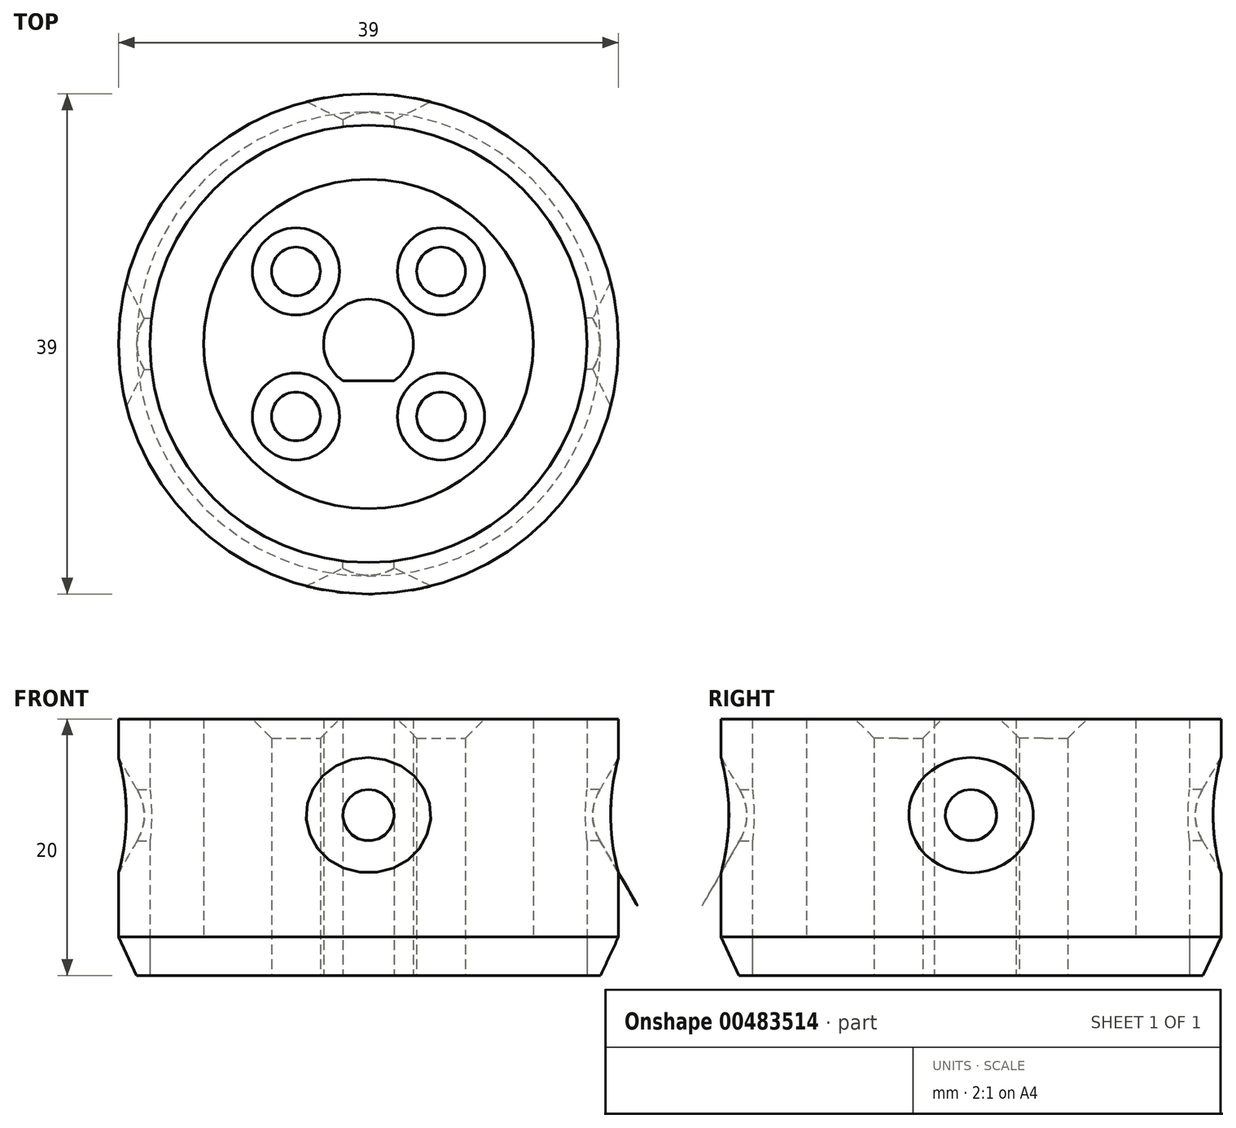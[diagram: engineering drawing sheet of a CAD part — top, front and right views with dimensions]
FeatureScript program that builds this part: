
annotation { "Feature Type Name" : "Feature", "Feature Type Description" : "" }
export const myFeature = defineFeature(function(context is Context, id is Id, definition is map)
    precondition{}
    {
        {
            var Q0;
            Q0=qCreatedBy(makeId("Top.planeOp"),FACE);
            var sketch = newSketch(context, id + "F0", { "sketchPlane" : qUnion([Q0])});
            skCircle(sketch, "E0", {"center": v(0, 0) * mm, "radius": 17.05 * mm});
            skCircle(sketch, "E1", {"center": v(0, 0) * mm, "radius": 3.35 * mm});
            skLineSegment(sketch, "E2", {"start": v(-2.3, -2.44) * mm, "end": v(1.68, -2.9) * mm});
            skSolve(sketch);
        }
        {
            var Q0;
            Q0=makeQuery(id+"F0.imprint","IMPRINT",FACE,{"disambiguationData":[TD([[makeQuery(id+"F0.imprint","IMPRINT",EDGE,{"derivedFrom":sQuery(id+"F0.wireOp",EDGE,"E0")}),1.0]])]});
            var sketch = newSketch(context, id + "F1", { "sketchPlane" : qUnion([Q0])});
            skCircle(sketch, "E3", {"center": v(0, 0) * mm, "radius": 19.5 * mm});
            skSolve(sketch);
        }
        {
            var Q0;
            Q0=makeQuery(id+"F1.imprint","IMPRINT",FACE,{"disambiguationData":[TD([[makeQuery(id+"F1.imprint","IMPRINT",EDGE,{"derivedFrom":sQuery(id+"F1.wireOp",EDGE,"E3")}),1.0]])]});
            var Q1;
            Q1=makeQuery(id+"F0.imprint","IMPRINT",FACE,{"disambiguationData":[TD([[makeQuery(id+"F0.imprint","IMPRINT",EDGE,{"derivedFrom":sQuery(id+"F0.wireOp",EDGE,"E0")}),1.0]])]});
            var Q2;
            {var subQ0=sQuery(id+"F0.wireOp",EDGE,"E2");Q2=makeQuery(id+"F0.imprint","IMPRINT",FACE,{"disambiguationData":[TD([[makeQuery(id+"F0.imprint","IMPRINT",EDGE,{"derivedFrom":subQ0}),1.0]])]});}
            var Q3;
            {var subQ0=sQuery(id+"F0.wireOp",EDGE,"E2");Q3=makeQuery(id+"F0.imprint","IMPRINT",FACE,{"disambiguationData":[TD([[makeQuery(id+"F0.imprint","IMPRINT",EDGE,{"derivedFrom":subQ0}),-1.0]])]});}
            extrude(context, id + "F2", {"entities" : qUnion([Q0, Q1, Q2, Q3]), "depth" : 20 * mm});
        }
        {
            var Q0;
            Q0=makeQuery(id+"F2.opExtrude","CAP_FACE",FACE,{"disambiguationData":[OSD([sQuery(id+"F0.wireOp",EDGE,"E0")])],"isStart":false});
            extrude(context, id + "F3", {"entities" : qUnion([Q0]), "operationType" : NewBodyOperationType.REMOVE, "oppositeDirection" : true, "depth" : 17 * mm});
        }
        {
            var Q0;
            Q0=makeQuery(id+"F2.opExtrude","CAP_FACE",FACE,{"disambiguationData":[OSD([sQuery(id+"F0.wireOp",EDGE,"E0")])],"isStart":true});
            var sketch = newSketch(context, id + "F4", { "sketchPlane" : qUnion([Q0])});
            skCircle(sketch, "E4", {"center": v(0, 0) * mm, "radius": 3.5 * mm});
            skLineSegment(sketch, "E5", {"start": v(-2, 2.87) * mm, "end": v(2, 2.87) * mm});
            skLineSegment(sketch, "E6", {"start": v(3.5, 0) * mm, "end": v(-3.5, 0) * mm, "construction": true});
            skSolve(sketch);
        }
        {
            var Q0;
            {var subQ0=sQuery(id+"F4.wireOp",EDGE,"E5");Q0=makeQuery(id+"F4.imprint","IMPRINT",FACE,{"disambiguationData":[TD([[makeQuery(id+"F4.imprint","IMPRINT",EDGE,{"derivedFrom":subQ0}),-1.0]])]});}
            extrude(context, id + "F5", {"entities" : qUnion([Q0]), "operationType" : NewBodyOperationType.REMOVE, "oppositeDirection" : true, "depth" : 9 * mm});
        }
        {
            var Q0;
            Q0=makeQuery(id+"F2.opExtrude","CAP_FACE",FACE,{"disambiguationData":[OSD([sQuery(id+"F0.wireOp",EDGE,"E0")])],"isStart":true});
            var sketch = newSketch(context, id + "F6", { "sketchPlane" : qUnion([Q0])});
            skLineSegment(sketch, "E7", {"start": v(0, 0) * mm, "end": v(-8, 0) * mm});
            skLineSegment(sketch, "E8", {"start": v(0, 0) * mm, "end": v(0, 8) * mm});
            skLineSegment(sketch, "E9", {"start": v(0, 0) * mm, "end": v(-5.66, 5.66) * mm});
            skLineSegment(sketch, "E10", {"start": v(0, 0) * mm, "end": v(5.66, -5.66) * mm});
            skLineSegment(sketch, "E11", {"start": v(0, 0) * mm, "end": v(-5.66, -5.66) * mm});
            skLineSegment(sketch, "E12", {"start": v(0, 0) * mm, "end": v(5.66, 5.66) * mm});
            skCircle(sketch, "E13", {"center": v(-5.66, 5.66) * mm, "radius": 1.9 * mm});
            skCircle(sketch, "E14", {"center": v(-5.66, -5.66) * mm, "radius": 1.9 * mm});
            skCircle(sketch, "E15", {"center": v(5.66, 5.66) * mm, "radius": 1.9 * mm});
            skCircle(sketch, "E16", {"center": v(5.66, -5.66) * mm, "radius": 1.9 * mm});
            skSolve(sketch);
        }
        {
            var Q0;
            Q0=makeQuery(id+"F6.imprint","IMPRINT",FACE,{"disambiguationData":[TD([[makeQuery(id+"F6.imprint","IMPRINT",EDGE,{"derivedFrom":sQuery(id+"F6.wireOp",EDGE,"E13")}),1.0]])]});
            var Q1;
            Q1=makeQuery(id+"F6.imprint","IMPRINT",FACE,{"disambiguationData":[TD([[makeQuery(id+"F6.imprint","IMPRINT",EDGE,{"derivedFrom":sQuery(id+"F6.wireOp",EDGE,"E14")}),1.0]])]});
            var Q2;
            Q2=makeQuery(id+"F6.imprint","IMPRINT",FACE,{"disambiguationData":[TD([[makeQuery(id+"F6.imprint","IMPRINT",EDGE,{"derivedFrom":sQuery(id+"F6.wireOp",EDGE,"E15")}),1.0]])]});
            var Q3;
            Q3=makeQuery(id+"F6.imprint","IMPRINT",FACE,{"disambiguationData":[TD([[makeQuery(id+"F6.imprint","IMPRINT",EDGE,{"derivedFrom":sQuery(id+"F6.wireOp",EDGE,"E16")}),1.0]])]});
            extrude(context, id + "F7", {"entities" : qUnion([Q0, Q1, Q2, Q3]), "operationType" : NewBodyOperationType.REMOVE, "oppositeDirection" : true, "depth" : 9 * mm});
        }
        {
            var Q0;
            Q0=qCreatedBy(makeId("Front.planeOp"),FACE);
            var sketch = newSketch(context, id + "F8", { "sketchPlane" : qUnion([Q0])});
            skLineSegment(sketch, "E17", {"start": v(0, 0) * mm, "end": v(0, 25) * mm});
            skCircle(sketch, "E18", {"center": v(0, 12.5) * mm, "radius": 2 * mm});
            skSolve(sketch);
        }
        {
            var Q0;
            Q0=qSketchRegion(id+"F8",true);
            extrude(context, id + "F9", {"entities" : qUnion([Q0]), "operationType" : NewBodyOperationType.REMOVE, "endBound" : BoundingType.THROUGH_ALL, "oppositeDirection" : true, "depth" : 25 * mm});
        }
        {
            var Q0;
            Q0=qCreatedBy(makeId("Front.planeOp"),FACE);
            var sketch = newSketch(context, id + "F10", { "sketchPlane" : qUnion([Q0])});
            skLineSegment(sketch, "E19", {"start": v(0, 0) * mm, "end": v(0, 25) * mm});
            skCircle(sketch, "E20", {"center": v(0, 12.5) * mm, "radius": 2 * mm});
            skSolve(sketch);
        }
        {
            var Q0;
            Q0=qSketchRegion(id+"F10",true);
            extrude(context, id + "F11", {"entities" : qUnion([Q0]), "operationType" : NewBodyOperationType.REMOVE, "endBound" : BoundingType.THROUGH_ALL, "depth" : 25 * mm});
        }
        {
            var Q0;
            Q0=qCreatedBy(makeId("Right.planeOp"),FACE);
            var sketch = newSketch(context, id + "F12", { "sketchPlane" : qUnion([Q0])});
            skLineSegment(sketch, "E21", {"start": v(0, 0) * mm, "end": v(0, 25) * mm});
            skCircle(sketch, "E22", {"center": v(0, 12.5) * mm, "radius": 2 * mm});
            skSolve(sketch);
        }
        {
            var Q0;
            Q0=qSketchRegion(id+"F12",true);
            extrude(context, id + "F13", {"entities" : qUnion([Q0]), "operationType" : NewBodyOperationType.REMOVE, "endBound" : BoundingType.THROUGH_ALL, "oppositeDirection" : true, "depth" : 25 * mm});
        }
        {
            var Q0;
            Q0=qCreatedBy(makeId("Right.planeOp"),FACE);
            var sketch = newSketch(context, id + "F14", { "sketchPlane" : qUnion([Q0])});
            skLineSegment(sketch, "E23", {"start": v(0, 0) * mm, "end": v(0, 25) * mm});
            skCircle(sketch, "E24", {"center": v(0, 12.5) * mm, "radius": 2 * mm});
            skSolve(sketch);
        }
        {
            var Q0;
            Q0=qSketchRegion(id+"F14",true);
            extrude(context, id + "F15", {"entities" : qUnion([Q0]), "operationType" : NewBodyOperationType.REMOVE, "endBound" : BoundingType.THROUGH_ALL, "depth" : 25 * mm});
        }
        {
            var Q0;
            Q0=makeQuery(id+"F3.boolean.opBoolean","COPY",FACE,{"derivedFrom":makeQuery(id+"F3.opExtrude","CAP_FACE",FACE,{"disambiguationData":[OSD([sQuery(id+"F0.wireOp",EDGE,"E0")])],"isStart":false})});
            var sketch = newSketch(context, id + "F16", { "sketchPlane" : qUnion([Q0])});
            skCircle(sketch, "E25", {"center": v(0, 0) * mm, "radius": 12.85 * mm});
            skSolve(sketch);
        }
        {
            var Q0;
            Q0=makeQuery(id+"F16.imprint","IMPRINT",FACE,{"disambiguationData":[TD([[makeQuery(id+"F16.imprint","IMPRINT",EDGE,{"derivedFrom":sQuery(id+"F16.wireOp",EDGE,"E25")}),1.0]])]});
            extrude(context, id + "F17", {"entities" : qUnion([Q0]), "operationType" : NewBodyOperationType.ADD, "depth" : 17 * mm});
        }
        {
            var Q0;
            Q0=makeQuery(id+"F17.opExtrude","CAP_EDGE",EDGE,{"disambiguationData":[OSD([sQuery(id+"F0.wireOp",EDGE,"E0"),sQuery(id+"F6.wireOp",EDGE,"E13")])],"isStart":false});
            var Q1;
            Q1=makeQuery(id+"F17.opExtrude","CAP_EDGE",EDGE,{"disambiguationData":[OSD([sQuery(id+"F0.wireOp",EDGE,"E0"),sQuery(id+"F6.wireOp",EDGE,"E14")])],"isStart":false});
            var Q2;
            Q2=makeQuery(id+"F17.opExtrude","CAP_EDGE",EDGE,{"disambiguationData":[OSD([sQuery(id+"F0.wireOp",EDGE,"E0"),sQuery(id+"F6.wireOp",EDGE,"E16")])],"isStart":false});
            var Q3;
            Q3=makeQuery(id+"F17.opExtrude","CAP_EDGE",EDGE,{"disambiguationData":[OSD([sQuery(id+"F0.wireOp",EDGE,"E0"),sQuery(id+"F6.wireOp",EDGE,"E15")])],"isStart":false});
            chamfer(context, id + "F18", {"entities" : qUnion([Q0, Q1, Q2, Q3]), "width" : 1.5 * mm, "tangentPropagation" : true});
        }
        {
            var Q0;
            Q0=makeQuery(id+"F13.boolean.opBoolean","INTERSECT",EDGE,{"derivedFrom":[makeQuery(id+"F2.opExtrude","SWEPT_FACE",FACE,{"disambiguationData":[OSD([sQuery(id+"F1.wireOp",EDGE,"E3")])]}),makeQuery(id+"F13.opExtrude","SWEPT_FACE",FACE,{"disambiguationData":[OSD([sQuery(id+"F12.wireOp",EDGE,"E22")])]})]});
            var Q1;
            Q1=makeQuery(id+"F9.boolean.opBoolean","INTERSECT",EDGE,{"derivedFrom":[makeQuery(id+"F2.opExtrude","SWEPT_FACE",FACE,{"disambiguationData":[OSD([sQuery(id+"F1.wireOp",EDGE,"E3")])]}),makeQuery(id+"F9.opExtrude","SWEPT_FACE",FACE,{"disambiguationData":[OSD([sQuery(id+"F8.wireOp",EDGE,"E18")])]})]});
            var Q2;
            Q2=makeQuery(id+"F11.boolean.opBoolean","INTERSECT",EDGE,{"derivedFrom":[makeQuery(id+"F2.opExtrude","SWEPT_FACE",FACE,{"disambiguationData":[OSD([sQuery(id+"F1.wireOp",EDGE,"E3")])]}),makeQuery(id+"F11.opExtrude","SWEPT_FACE",FACE,{"disambiguationData":[OSD([sQuery(id+"F10.wireOp",EDGE,"E20")])]})]});
            var Q3;
            Q3=makeQuery(id+"F15.boolean.opBoolean","INTERSECT",EDGE,{"derivedFrom":[makeQuery(id+"F2.opExtrude","SWEPT_FACE",FACE,{"disambiguationData":[OSD([sQuery(id+"F1.wireOp",EDGE,"E3")])]}),makeQuery(id+"F15.opExtrude","SWEPT_FACE",FACE,{"disambiguationData":[OSD([sQuery(id+"F14.wireOp",EDGE,"E24")])]})]});
            chamfer(context, id + "F19", {"entities" : qUnion([Q0, Q1, Q2, Q3]), "chamferType" : ChamferType.OFFSET_ANGLE, "width" : 2.5 * mm, "oppositeDirection" : false, "angle" : 30 * degree, "tangentPropagation" : true});
        }
        {
            var Q0;
            Q0=makeQuery(id+"F2.opExtrude","CAP_EDGE",EDGE,{"disambiguationData":[OSD([sQuery(id+"F1.wireOp",EDGE,"E3")])],"isStart":true});
            chamfer(context, id + "F20", {"entities" : qUnion([Q0]), "chamferType" : ChamferType.OFFSET_ANGLE, "width" : 3 * mm, "oppositeDirection" : false, "angle" : 25 * degree, "tangentPropagation" : true});
        }
    });
